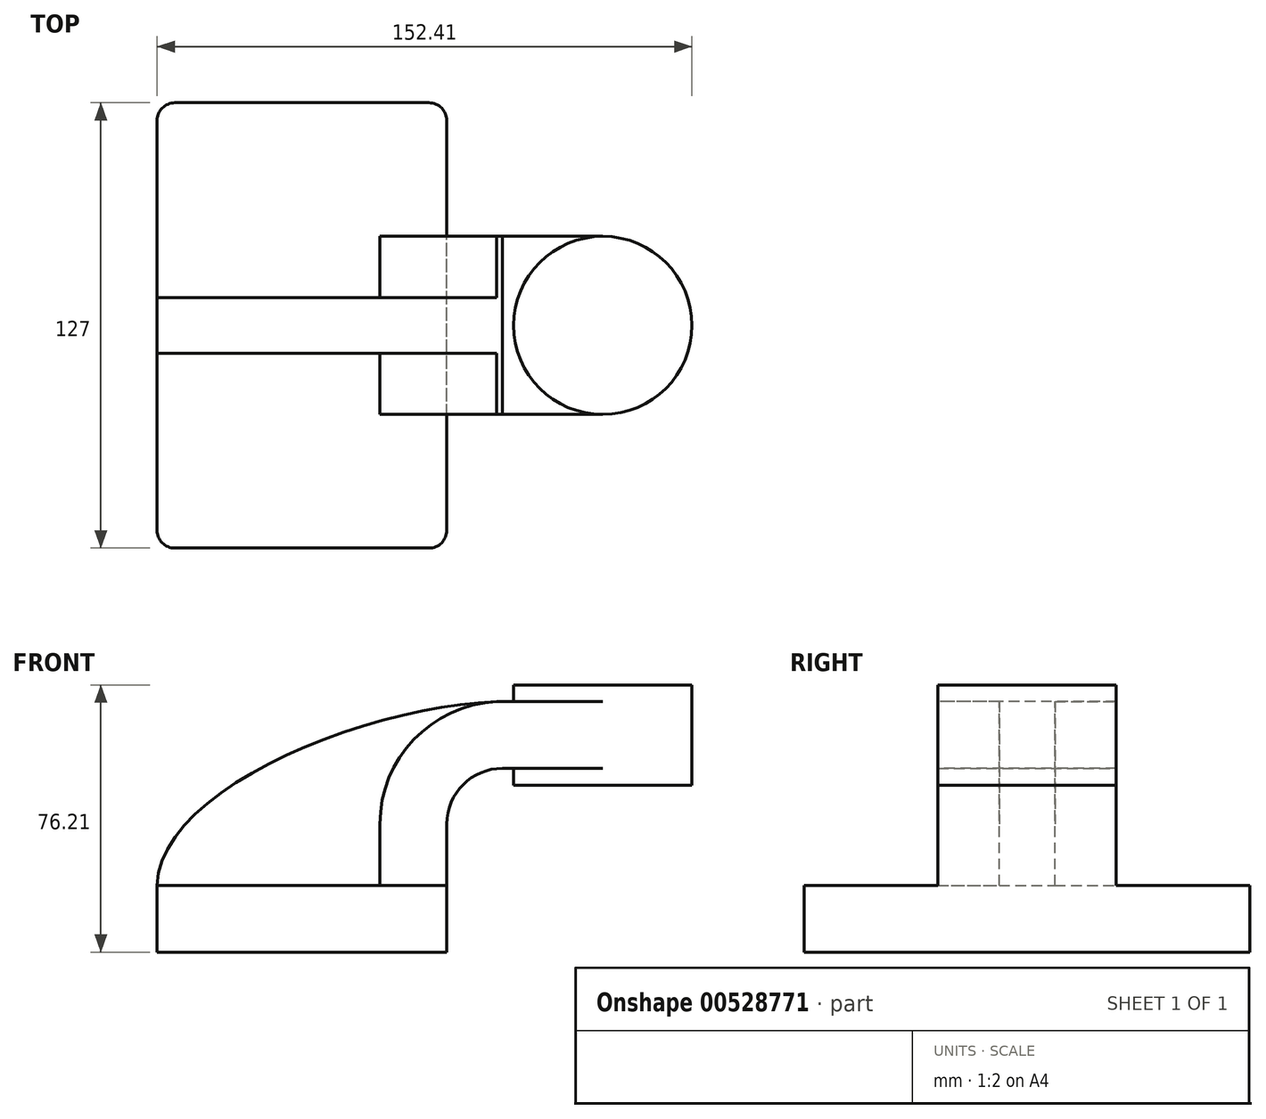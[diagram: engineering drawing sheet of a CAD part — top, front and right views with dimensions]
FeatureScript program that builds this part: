
annotation { "Feature Type Name" : "Feature", "Feature Type Description" : "" }
export const myFeature = defineFeature(function(context is Context, id is Id, definition is map)
    precondition{}
    {
        {
            var Q0;
            Q0=qCreatedBy(makeId("Front.planeOp"),FACE);
            var sketch = newSketch(context, id + "F0", { "sketchPlane" : qUnion([Q0])});
            skLineSegment(sketch, "E0.bottom", {"start": v(41.27, -9.52) * mm, "end": v(-41.27, -9.53) * mm});
            skLineSegment(sketch, "E0.top", {"start": v(41.27, 9.53) * mm, "end": v(-41.28, 9.52) * mm});
            skLineSegment(sketch, "E0.left", {"start": v(41.28, -9.52) * mm, "end": v(41.27, 9.53) * mm});
            skLineSegment(sketch, "E0.right", {"start": v(-41.27, -9.53) * mm, "end": v(-41.28, 9.52) * mm});
            skPoint(sketch, "E0.middle", {"position": v(0, 0) * mm});
            skLineSegment(sketch, "E1.bottom", {"start": v(111.13, 38.1) * mm, "end": v(60.33, 38.1) * mm});
            skLineSegment(sketch, "E1.top", {"start": v(111.13, 66.68) * mm, "end": v(60.33, 66.68) * mm});
            skLineSegment(sketch, "E1.left", {"start": v(111.12, 38.1) * mm, "end": v(111.12, 66.68) * mm});
            skLineSegment(sketch, "E1.right", {"start": v(60.33, 38.1) * mm, "end": v(60.33, 66.68) * mm});
            skPoint(sketch, "E1.middle", {"position": v(85.73, 52.39) * mm});
            skLineSegment(sketch, "E2", {"start": v(41.27, 9.53) * mm, "end": v(41.27, 27) * mm});
            skArc(sketch, "E3", {"start": v(41.27, 27) * mm, "mid": v(45.92, 38.23) * mm, "end": v(57.15, 42.88) * mm});
            skLineSegment(sketch, "E4", {"start": v(57.15, 42.88) * mm, "end": v(85.72, 42.88) * mm});
            skLineSegment(sketch, "E5.0", {"start": v(57.15, 61.93) * mm, "end": v(85.72, 61.93) * mm});
            skArc(sketch, "E5.1", {"start": v(22.22, 27) * mm, "mid": v(32.45, 51.7) * mm, "end": v(57.15, 61.93) * mm});
            skLineSegment(sketch, "E5.2", {"start": v(22.22, 9.52) * mm, "end": v(22.22, 27) * mm});
            skLineSegment(sketch, "E6", {"start": v(85.73, 66.68) * mm, "end": v(85.73, 38.1) * mm});
            skLineSegment(sketch, "E7", {"start": v(85.73, 38.1) * mm, "end": v(85.73, 42.88) * mm});
            skFitSpline(sketch, "E8", {"points": [v(-41.28, 9.53) * mm, v(57.15, 61.93) * mm], "startDerivative": vector(1.67, 82.62) * mm, "endDerivative": vector(113.47, 1.76) * mm});
            skSolve(sketch);
        }
        {
            var Q0;
            Q0=makeQuery(id+"F0.imprint","IMPRINT",FACE,{"disambiguationData":[TD([[makeQuery(id+"F0.imprint","IMPRINT",EDGE,{"derivedFrom":sQuery(id+"F0.wireOp",EDGE,"E0.bottom")}),-1.0]])]});
            extrude(context, id + "F1", {"entities" : qUnion([Q0]), "endBound" : BoundingType.SYMMETRIC, "depth" : 127 * mm, "offsetDistance" : 25.4 * mm});
        }
        {
            var Q0;
            {var subQ1=sQuery(id+"F0.wireOp",EDGE,"E2");Q0=makeQuery(id+"F0.imprint","IMPRINT",FACE,{"disambiguationData":[TD([[makeQuery(id+"F0.imprint","IMPRINT",EDGE,{"derivedFrom":subQ1}),1.0]])]});}
            var Q1;
            {var subQ0=sQuery(id+"F0.wireOp",EDGE,"E4");var subQ1=sQuery(id+"F0.wireOp",EDGE,"E1.right");var subQ2=makeQuery(id+"F0.imprint","INTERSECT",VERTEX,{"derivedFrom":[subQ1,subQ0]});Q1=makeQuery(id+"F0.imprint","IMPRINT",FACE,{"disambiguationData":[TD([[makeQuery(id+"F0.imprint","IMPRINT",EDGE,{"disambiguationData":[TD([[subQ2,-1.0]])],"derivedFrom":subQ1}),-1.0]])]});}
            extrude(context, id + "F2", {"entities" : qUnion([Q0, Q1]), "operationType" : NewBodyOperationType.ADD, "endBound" : BoundingType.SYMMETRIC, "depth" : 50.8 * mm, "offsetDistance" : 25.4 * mm});
        }
        {
            var Q0;
            {var subQ3=sQuery(id+"F0.wireOp",EDGE,"E5.2");Q0=makeQuery(id+"F0.imprint","IMPRINT",FACE,{"disambiguationData":[TD([[makeQuery(id+"F0.imprint","IMPRINT",EDGE,{"derivedFrom":subQ3}),1.0]])]});}
            extrude(context, id + "F3", {"entities" : qUnion([Q0]), "operationType" : NewBodyOperationType.ADD, "endBound" : BoundingType.SYMMETRIC, "depth" : 15.88 * mm, "offsetDistance" : 25.4 * mm});
        }
        {
            var Q0;
            {var subQ0=sQuery(id+"F0.wireOp",EDGE,"E1.left");Q0=makeQuery(id+"F0.imprint","IMPRINT",FACE,{"disambiguationData":[TD([[makeQuery(id+"F0.imprint","IMPRINT",EDGE,{"derivedFrom":subQ0}),1.0]])]});}
            var Q1;
            Q1=sQuery(id+"F0.wireOp",EDGE,"E6");
            revolve(context, id + "F4", {"operationType" : NewBodyOperationType.ADD, "entities" : qUnion([Q0]), "axis" : qUnion([Q1]), "revolveType" : RevolveType.FULL});
        }
        {
            var Q0;
            Q0=makeQuery(id+"F1.opExtrude","CAP_EDGE",EDGE,{"disambiguationData":[OSD([sQuery(id+"F0.wireOp",EDGE,"E0.left")])],"isStart":false});
            var Q1;
            Q1=makeQuery(id+"F1.opExtrude","CAP_EDGE",EDGE,{"disambiguationData":[OSD([sQuery(id+"F0.wireOp",EDGE,"E0.right")])],"isStart":false});
            var Q2;
            Q2=makeQuery(id+"F1.opExtrude","CAP_EDGE",EDGE,{"disambiguationData":[OSD([sQuery(id+"F0.wireOp",EDGE,"E0.right")])],"isStart":true});
            var Q3;
            Q3=makeQuery(id+"F1.opExtrude","CAP_EDGE",EDGE,{"disambiguationData":[OSD([sQuery(id+"F0.wireOp",EDGE,"E0.left")])],"isStart":true});
            fillet(context, id + "F5", {"entities" : qUnion([Q0, Q1, Q2, Q3]), "radius" : 5.08 * mm, "tangentPropagation" : true, "allowEdgeOverflow" : false});
        }
    });
